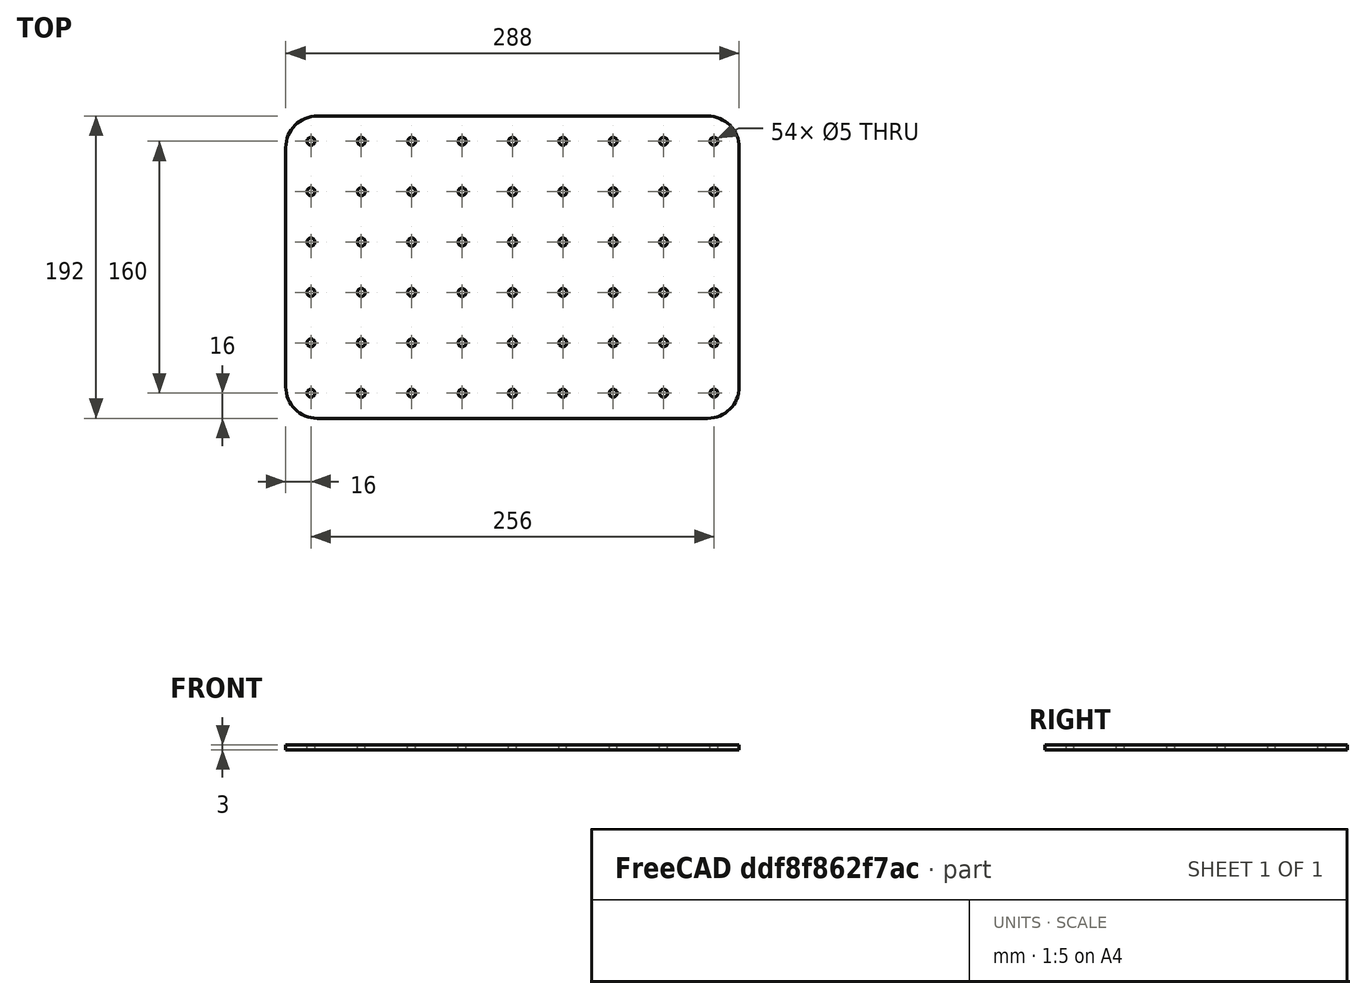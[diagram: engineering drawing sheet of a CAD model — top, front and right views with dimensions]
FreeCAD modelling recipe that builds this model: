
FCSTD DOCUMENT  (FreeCAD 0.21R33771 (Git))
Label: 32-grid-Base-Plate
License: All rights reserved
LicenseURL: http://en.wikipedia.org/wiki/All_rights_reserved
objects: TechDraw::DrawViewDimension×9, TechDraw::DrawProjGroupItem×3, Sketcher::SketchObject×2, PartDesign::LinearPattern×2, TechDraw::DrawSVGTemplate×2, TechDraw::DrawPage×2, App::TextDocument×1, Spreadsheet::Sheet×1, PartDesign::Pad×1, PartDesign::Hole×1, PartDesign::MultiTransform×1, PartDesign::Body×1, TechDraw::DrawProjGroup×1, TechDraw::DrawViewBalloon×1, TechDraw::DrawViewPart×1, TechDraw::DrawViewAnnotation×1
note: 26 computed .brp shape members not serialized (recipe doc carries the construction recipe); baked Part::Feature solids carry a one-line shape summary decoded from their .brp

FEATURE [Sketcher::SketchObject] Sketch  label="main-base-sketch"
  FullyConstrained = true
  MapMode = 5
  Support = -> [XY_Plane]
  expr: Constraints[16] = Spreadsheet.base_grid * Spreadsheet.vertical
  expr: Constraints[17] = Spreadsheet.base_grid * Spreadsheet.horizontal
  expr: Constraints[18] = Spreadsheet.corner_rad
  sketch-geometry (8):
    g0: LineSegment StartX=-124 StartY=96 StartZ=0 EndX=124 EndY=96 EndZ=0
    g1: LineSegment StartX=144 StartY=76 StartZ=0 EndX=144 EndY=-76 EndZ=0
    g2: LineSegment StartX=124 StartY=-96 StartZ=0 EndX=-124 EndY=-96 EndZ=0
    g3: LineSegment StartX=-144 StartY=-76 StartZ=0 EndX=-144 EndY=76 EndZ=0
    g4: ArcOfCircle CenterX=124 CenterY=-76 CenterZ=0 NormalX=0 NormalY=0 NormalZ=1 AngleXU=0 Radius=20 StartAngle=4.71239 EndAngle=6.28319
    g5: ArcOfCircle CenterX=-124 CenterY=76 CenterZ=0 NormalX=0 NormalY=0 NormalZ=1 AngleXU=0 Radius=20 StartAngle=1.5708 EndAngle=3.14159
    g6: ArcOfCircle CenterX=124 CenterY=76 CenterZ=0 NormalX=0 NormalY=0 NormalZ=1 AngleXU=0 Radius=20 StartAngle=3e-16 EndAngle=1.5708
    g7: ArcOfCircle CenterX=-124 CenterY=-76 CenterZ=0 NormalX=0 NormalY=0 NormalZ=1 AngleXU=0 Radius=20 StartAngle=3.14159 EndAngle=4.71239
  constraints (19):
    c: Horizontal(g0)
    c: Horizontal(g2)
    c: Vertical(g1)
    c: Vertical(g3)
    c: Tangent(g1,g4) = 1.5708
    c: Tangent(g2,g4) = 1.5708
    c: Tangent(g3,g5) = 1.5708
    c: Tangent(g0,g5) = 1.5708
    c: Tangent(g0,g6) = 1.5708
    c: Tangent(g1,g6) = 1.5708
    c: Tangent(g3,g7) = 1.5708
    c: Tangent(g2,g7) = 1.5708
    c: Equal(g6,g4)
    c: Equal(g4,g7)
    c: Equal(g7,g5)
    c: Symmetric(g4,g5,g-1)
    c: DistanceY(g2,g0) = 192
    c: DistanceX(g3,g1) = 288
    c: Radius(g6) = 20
FEATURE [App::TextDocument] Text_document  label="notes"
  Text = 32mm Grid to be later transferred into different parametric options
FEATURE [Spreadsheet::Sheet] Spreadsheet  label="Parameters"
  cells = A1='Ref; B1='Value; C1='Description; A2='grid_boring; B2(grid_boring)=5; C2='main bore holes reference for grid; A3='corner_rad; B3(corner_rad)=20; C3='radius of the base plate corners; A4='base_grid; B4(base_grid)=32; C4='grid standard reference (standard 32mm); A5='thickness; B5(thickness)=3; C5='base plate thickness of material; A6='horizontal; B6(horizontal)=9; C6='holes horizonal; A7='vertical; B7(vertical)=6; C7='holes vertical; A8='grid_factor; B8(grid_factor)=1; C8='change the base grid reference for parametric designs
FEATURE [PartDesign::Pad] Pad
  Direction = (0,0,1)
  Length = 3
  Length2 = 10
  Profile = -> Sketch
  ReferenceAxis = -> Sketch [N_Axis]
  Type = 0
  expr: Length = Spreadsheet.thickness
FEATURE [Sketcher::SketchObject] Sketch001  label="bore-hole-sketch"
  FullyConstrained = true
  MapMode = 5
  Support = -> [XY_Plane]
  expr: Constraints[16] = Sketch.Constraints[16]
  expr: Constraints[17] = Sketch.Constraints[17]
  expr: Constraints[18] = Sketch.Constraints[18]
  expr: Constraints[19] = Spreadsheet.base_grid * Spreadsheet.grid_factor / 2
  expr: Constraints[20] = Spreadsheet.base_grid * Spreadsheet.grid_factor / 2
  expr: Constraints[21] = Spreadsheet.grid_boring
  sketch-geometry (9):
    g0: LineSegment StartX=-124 StartY=96 StartZ=0 EndX=124 EndY=96 EndZ=0
    g1: LineSegment StartX=144 StartY=76 StartZ=0 EndX=144 EndY=-76 EndZ=0
    g2: LineSegment StartX=124 StartY=-96 StartZ=0 EndX=-124 EndY=-96 EndZ=0
    g3: LineSegment StartX=-144 StartY=-76 StartZ=0 EndX=-144 EndY=76 EndZ=0
    g4: ArcOfCircle CenterX=124 CenterY=-76 CenterZ=0 NormalX=0 NormalY=0 NormalZ=1 AngleXU=0 Radius=20 StartAngle=4.71239 EndAngle=6.28319
    g5: ArcOfCircle CenterX=-124 CenterY=76 CenterZ=0 NormalX=0 NormalY=0 NormalZ=1 AngleXU=0 Radius=20 StartAngle=1.5708 EndAngle=3.14159
    g6: ArcOfCircle CenterX=124 CenterY=76 CenterZ=0 NormalX=0 NormalY=0 NormalZ=1 AngleXU=0 Radius=20 StartAngle=2e-16 EndAngle=1.5708
    g7: ArcOfCircle CenterX=-124 CenterY=-76 CenterZ=0 NormalX=0 NormalY=0 NormalZ=1 AngleXU=0 Radius=20 StartAngle=3.14159 EndAngle=4.71239
    g8: Circle CenterX=128 CenterY=80 CenterZ=0 NormalX=0 NormalY=0 NormalZ=1 AngleXU=0 Radius=2.5
  constraints (22):
    c: Horizontal(g0)
    c: Horizontal(g2)
    c: Vertical(g1)
    c: Vertical(g3)
    c: Tangent(g1,g4) = 1.5708
    c: Tangent(g2,g4) = 1.5708
    c: Tangent(g3,g5) = 1.5708
    c: Tangent(g0,g5) = 1.5708
    c: Tangent(g0,g6) = 1.5708
    c: Tangent(g1,g6) = 1.5708
    c: Tangent(g3,g7) = 1.5708
    c: Tangent(g2,g7) = 1.5708
    c: Equal(g6,g4)
    c: Equal(g4,g7)
    c: Equal(g7,g5)
    c: Symmetric(g4,g5,g-1)
    c: DistanceY(g2,g0) = 192
    c: DistanceX(g3,g1) = 288
    c: Radius(g6) = 20
    c: DistanceY(g8,g0) = 16
    c: DistanceX(g8,g1) = 16
    c: Diameter(g8) = 5
FEATURE [PartDesign::Hole] Hole  label="Base-Bore-Hole"
  BaseFeature = -> Pad
  CustomThreadClearance = 0
  Depth = 699.261
  DepthType = 1
  Diameter = 5
  DrillForDepth = false
  DrillPoint = 1
  DrillPointAngle = 118
  HoleCutCountersinkAngle = 90
  HoleCutCustomValues = false
  HoleCutDepth = 0
  HoleCutDiameter = 6.1
  HoleCutType = 0
  ModelThread = false
  Profile = -> Sketch001
  Reversed = true
  Tapered = false
  TaperedAngle = 90
  ThreadClass = 0
  ThreadDepth = 699.261
  ThreadDepthType = 0
  ThreadDirection = 0
  ThreadFit = 0
  ThreadSize = 0
  ThreadType = 0
  Threaded = false
  UseCustomThreadClearance = false
  expr: Diameter = Spreadsheet.grid_boring
FEATURE [PartDesign::LinearPattern] LinearPattern
  Direction = -> Sketch001 [H_Axis]
  Length = 256
  Occurrences = 9
  Reversed = true
  expr: Length = Spreadsheet.base_grid * Spreadsheet.grid_factor * (Spreadsheet.horizontal / Spreadsheet.grid_factor - 1)
  expr: Occurrences = Spreadsheet.horizontal / Spreadsheet.grid_factor
FEATURE [PartDesign::LinearPattern] LinearPattern001
  Direction = -> Sketch001 [V_Axis]
  Length = 160
  Occurrences = 6
  Reversed = true
  expr: Length = Spreadsheet.base_grid * Spreadsheet.grid_factor * (Spreadsheet.vertical / Spreadsheet.grid_factor - 1)
  expr: Occurrences = Spreadsheet.vertical / Spreadsheet.grid_factor
FEATURE [PartDesign::MultiTransform] MultiTransform  label="Base-Grid-Bore-Holes"
  BaseFeature = -> Hole
  Originals = -> [Hole]
  Transformations = -> [LinearPattern,LinearPattern001]
FEATURE [PartDesign::Body] Body  label="Base-Plate"
  Group = -> [Sketch,Pad,Sketch001,Hole,MultiTransform,LinearPattern,LinearPattern001]
  Origin = -> Origin
  Tip = -> MultiTransform
FEATURE [TechDraw::DrawSVGTemplate] Template001  label="Base Plate Page1"
  EditableTexts = AUTHOR_NAME=Timm Wille; DRAWING_TITLE=32mm Grid Base Plate; FC-DATE=26.09.2024; FC-REV=v0.1-4; FC-SC=1/2; FC-SH=1 / 1; FC-SI=A3; FreeCAD_DRAWING=FreeCAD DRAWING; SI-1=in mm; SI-6=LICENSE: CC-BY-SA 4.0
  Height = 297
  Orientation = 1
  Template = <path>
  Width = 420
FEATURE [TechDraw::DrawProjGroupItem] ProjItem  label="Front"
  CoarseView = false
  Direction = (0,-1,0)
  Focus = 100
  HardHidden = false
  IsoCount = 0
  IsoHidden = false
  IsoVisible = false
  LockPosition = true
  Perspective = false
  Rotation = 0
  RotationVector = (1,0,0)
  Scale = 0.5
  ScaleType = 2
  ScrubCount = 0
  SeamHidden = false
  SeamVisible = false
  SmoothHidden = false
  SmoothVisible = true
  Source = -> [Body]
  Type = 0
  X = 0
  XDirection = (-1,0,1e-16)
  Y = 0
FEATURE [TechDraw::DrawProjGroupItem] ProjItem002  label="FrontTopRight"
  CoarseView = false
  Direction = (-0.57735,-0.57735,-0.57735)
  Focus = 100
  HardHidden = false
  IsoCount = 0
  IsoHidden = false
  IsoVisible = false
  LockPosition = true
  Perspective = false
  Rotation = 0
  RotationVector = (1,0,0)
  ScaleType = 2
  ScrubCount = 0
  SeamHidden = false
  SeamVisible = false
  SmoothHidden = false
  SmoothVisible = true
  Source = -> [Body]
  Type = 7
  X = -176.645
  XDirection = (-0.707107,0.707107,1e-16)
  Y = -177.1
FEATURE [TechDraw::DrawViewDimension] Dimension002
  AngleOverride = false
  Arbitrary = false
  ArbitraryTolerances = false
  EqualTolerance = true
  ExtensionAngle = 0
  FormatSpec = %.2w
  FormatSpecOverTolerance = %+.2w
  FormatSpecUnderTolerance = %+.2w
  Inverted = false
  LineAngle = 0
  LockPosition = false
  MeasureType = 1
  OverTolerance = 0
  References2D = -> [ProjItem]
  Rotation = 0
  ScaleType = 0
  TheoreticalExact = false
  Type = 2
  UnderTolerance = 0
  X = 79.6749
  Y = 11.0925
FEATURE [TechDraw::DrawProjGroupItem] ProjItem001  label="Top"
  CoarseView = false
  Direction = (-1e-16,0,-1)
  Focus = 100
  HardHidden = false
  IsoCount = 0
  IsoHidden = false
  IsoVisible = false
  LockPosition = false
  Perspective = false
  Rotation = 0
  RotationVector = (1,0,0)
  Scale = 0.5
  ScaleType = 2
  ScrubCount = 0
  SeamHidden = false
  SeamVisible = false
  SmoothHidden = false
  SmoothVisible = true
  Source = -> [Body]
  Type = 4
  X = 0
  XDirection = (-1,0,1e-16)
  Y = -63.75
FEATURE [TechDraw::DrawProjGroup] ProjGroup
  Anchor = -> ProjItem
  AutoDistribute = true
  LockPosition = false
  ProjectionType = 0
  Rotation = 0
  Scale = 0.5
  ScaleType = 2
  Source = -> [Body]
  Views = -> [ProjItem,ProjItem001,ProjItem002]
  X = 301.061
  Y = 257.02
  spacingX = 15
  spacingY = 15
FEATURE [TechDraw::DrawViewDimension] Dimension
  AngleOverride = false
  Arbitrary = false
  ArbitraryTolerances = false
  EqualTolerance = true
  ExtensionAngle = 0
  FormatSpec = %.2w
  FormatSpecOverTolerance = %+.2w
  FormatSpecUnderTolerance = %+.2w
  Inverted = false
  LineAngle = 0
  LockPosition = false
  MeasureType = 1
  OverTolerance = 0
  References2D = -> [ProjItem001]
  Rotation = 0
  ScaleType = 0
  TheoreticalExact = false
  Type = 1
  UnderTolerance = 0
  X = -0.47588
  Y = -74.1283
FEATURE [TechDraw::DrawViewDimension] Dimension001
  AngleOverride = false
  Arbitrary = false
  ArbitraryTolerances = false
  EqualTolerance = true
  ExtensionAngle = 0
  FormatSpec = %.2w
  FormatSpecOverTolerance = %+.2w
  FormatSpecUnderTolerance = %+.2w
  Inverted = false
  LineAngle = 0
  LockPosition = false
  MeasureType = 1
  OverTolerance = 0
  References2D = -> [ProjItem001]
  Rotation = 0
  ScaleType = 0
  TheoreticalExact = false
  Type = 2
  UnderTolerance = 0
  X = 96.1846
  Y = 4.02918
FEATURE [TechDraw::DrawViewDimension] Dimension004
  AngleOverride = false
  Arbitrary = false
  ArbitraryTolerances = false
  EqualTolerance = true
  ExtensionAngle = 0
  FormatSpec = R%.2w
  FormatSpecOverTolerance = %+.2w
  FormatSpecUnderTolerance = %+.2w
  Inverted = false
  LineAngle = 0
  LockPosition = false
  MeasureType = 1
  OverTolerance = 0
  References2D = -> [ProjItem001]
  Rotation = 0
  ScaleType = 0
  TheoreticalExact = false
  Type = 4
  UnderTolerance = 0
  X = 88.321
  Y = -60.3052
FEATURE [TechDraw::DrawViewBalloon] Balloon
  BubbleShape = 6
  EndType = 0
  EndTypeScale = 1
  KinkLength = 5
  LockPosition = false
  OriginX = -102.96
  OriginY = -87.5189
  Rotation = 0
  ScaleType = 0
  ShapeScale = 1
  SourceView = -> ProjItem001
  Text = 32x32mm bore holes grid paddern
  TextWrapLen = -1
  X = 35.9411
  Y = -208.188
FEATURE [TechDraw::DrawSVGTemplate] Template
  Height = 297
  Orientation = 1
  Template = <path>
  Width = 420
FEATURE [TechDraw::DrawViewPart] View
  CoarseView = false
  Direction = (0,0,1)
  Focus = 100
  HardHidden = false
  IsoCount = 0
  IsoHidden = false
  IsoVisible = false
  LockPosition = false
  Perspective = false
  Rotation = 0
  ScaleType = 0
  ScrubCount = 0
  SeamHidden = false
  SeamVisible = false
  SmoothHidden = false
  SmoothVisible = true
  Source = -> [Body]
  X = 217.568
  XDirection = (1,0,0)
  Y = 155.059
FEATURE [TechDraw::DrawPage] Page  label="2D SVG Export"
  KeepUpdated = true
  NextBalloonIndex = 1
  ProjectionType = 0
  Template = -> Template
  Views = -> [View]
FEATURE [TechDraw::DrawViewDimension] Dimension005
  AngleOverride = false
  Arbitrary = false
  ArbitraryTolerances = false
  EqualTolerance = true
  ExtensionAngle = 0
  FormatSpec = ⌀%.2w
  FormatSpecOverTolerance = %+.2w
  FormatSpecUnderTolerance = %+.2w
  Inverted = false
  LineAngle = 0
  LockPosition = false
  MeasureType = 1
  OverTolerance = 0
  References2D = -> [ProjItem001]
  Rotation = 0
  ScaleType = 0
  TheoreticalExact = false
  Type = 5
  UnderTolerance = 0
  X = -87.8273
  Y = -40.8072
FEATURE [TechDraw::DrawViewDimension] Dimension006
  AngleOverride = false
  Arbitrary = false
  ArbitraryTolerances = false
  EqualTolerance = true
  ExtensionAngle = 0
  FormatSpec = %.2w
  FormatSpecOverTolerance = %+.2w
  FormatSpecUnderTolerance = %+.2w
  Inverted = false
  LineAngle = 0
  LockPosition = false
  MeasureType = 1
  OverTolerance = 0
  References2D = -> [ProjItem001]
  Rotation = 0
  ScaleType = 0
  TheoreticalExact = false
  Type = 2
  UnderTolerance = 0
  X = -81.3807
  Y = 35.234
FEATURE [TechDraw::DrawViewDimension] Dimension007
  AngleOverride = false
  Arbitrary = false
  ArbitraryTolerances = false
  EqualTolerance = true
  ExtensionAngle = 0
  FormatSpec = %.2w
  FormatSpecOverTolerance = %+.2w
  FormatSpecUnderTolerance = %+.2w
  Inverted = false
  LineAngle = 0
  LockPosition = false
  MeasureType = 1
  OverTolerance = 0
  References2D = -> [ProjItem001]
  Rotation = 0
  ScaleType = 0
  TheoreticalExact = false
  Type = 1
  UnderTolerance = 0
  X = -56.2447
  Y = 60.5153
FEATURE [TechDraw::DrawViewDimension] Dimension008
  AngleOverride = false
  Arbitrary = false
  ArbitraryTolerances = false
  EqualTolerance = true
  ExtensionAngle = 0
  FormatSpec = %.2w
  FormatSpecOverTolerance = %+.2w
  FormatSpecUnderTolerance = %+.2w
  Inverted = false
  LineAngle = 0
  LockPosition = false
  MeasureType = 1
  OverTolerance = 0
  References2D = -> [ProjItem001]
  Rotation = 0
  ScaleType = 0
  TheoreticalExact = false
  Type = 1
  UnderTolerance = 0
  X = -86.0528
  Y = -26.2855
FEATURE [TechDraw::DrawViewDimension] Dimension009
  AngleOverride = false
  Arbitrary = false
  ArbitraryTolerances = false
  EqualTolerance = true
  ExtensionAngle = 0
  FormatSpec = %.2w
  FormatSpecOverTolerance = %+.2w
  FormatSpecUnderTolerance = %+.2w
  Inverted = false
  LineAngle = 0
  LockPosition = false
  MeasureType = 1
  OverTolerance = 0
  References2D = -> [ProjItem001]
  Rotation = 0
  ScaleType = 0
  TheoreticalExact = false
  Type = 2
  UnderTolerance = 0
  X = -57.8297
  Y = -56.898
FEATURE [TechDraw::DrawViewAnnotation] Annotation
  Font = osifont
  LineSpace = 100
  LockPosition = false
  MaxWidth = -1
  Rotation = 0
  ScaleType = 0
  Text = Technical Drawing of the #ASKotec Modules Base Plate | 32x32mm grid paddern for Prototyping | packing and collections setups
  TextSize = 5
  TextStyle = 0
  X = 120.347
  Y = 202.608
FEATURE [TechDraw::DrawPage] Page001  label="A3-Technical Drawing"
  KeepUpdated = true
  NextBalloonIndex = 3
  ProjectionType = 0
  Template = -> Template001
  Views = -> [ProjGroup,Dimension,Dimension001,Dimension002,Dimension004,Balloon,Dimension005,Dimension006,Dimension007,Dimension008,Dimension009,Annotation]
note: 2 file-system paths scrubbed to <path> (originals preserved in the JSON sidecar)
